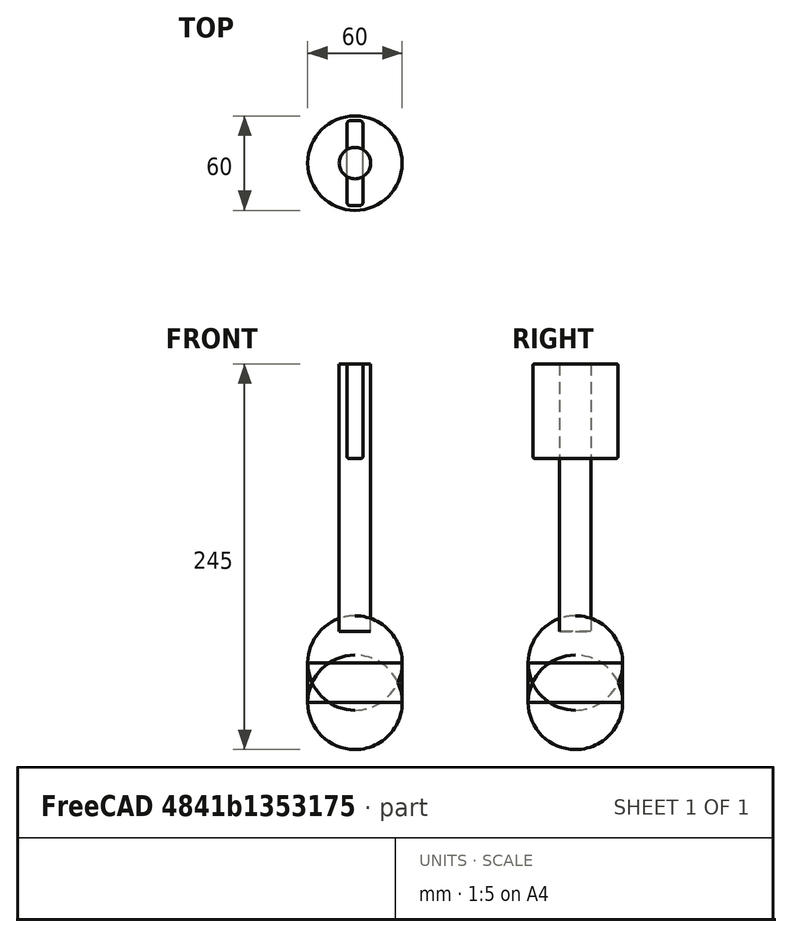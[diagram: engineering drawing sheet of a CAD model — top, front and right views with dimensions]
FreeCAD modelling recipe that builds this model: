
FCSTD DOCUMENT  (FreeCAD 0.20R29410 (Git))
Label: Spatule
License: All rights reserved
LicenseURL: http://en.wikipedia.org/wiki/All_rights_reserved
objects: Part::Sphere×2, Sketcher::SketchObject×1, PartDesign::Pad×1, PartDesign::Body×1, Part::Cylinder×1, Part::Box×1, Part::Fillet×1
note: 9 computed .brp shape members not serialized (recipe doc carries the construction recipe); baked Part::Feature solids carry a one-line shape summary decoded from their .brp

FEATURE [Sketcher::SketchObject] Sketch
  FullyConstrained = true
  MapMode = 5
  Support = -> [XY_Plane]
  sketch-geometry (1):
    g0: Circle CenterX=0 CenterY=0 CenterZ=0 NormalX=0 NormalY=0 NormalZ=1 AngleXU=0 Radius=30
  constraints (2):
    c: Coincident(g0,g-1)
    c: Radius(g0) = 30
FEATURE [PartDesign::Pad] Pad
  Direction = (0,0,1)
  Length = 25
  Length2 = 10
  Profile = -> Sketch
  ReferenceAxis = -> Sketch [N_Axis]
  Type = 0
FEATURE [PartDesign::Body] Body
  Group = -> [Sketch,Pad]
  Origin = -> Origin
  Tip = -> Pad
FEATURE [Part::Sphere] Sphere001
  Angle1 = -90
  Angle2 = 90
  Angle3 = 360
  AttacherType = Attacher::AttachEngine3D
  Placement = pos=(0,0,25) rot=(0,0,1;0rad)
  Radius = 30
FEATURE [Part::Cylinder] Cylinder
  Angle = 360
  AttacherType = Attacher::AttachEngine3D
  FirstAngle = 0
  Height = 170
  Placement = pos=(0,0,45) rot=(0,0,1;0rad)
  Radius = 10
  SecondAngle = 0
FEATURE [Part::Box] Box  label="Cube"
  AttacherType = Attacher::AttachEngine3D
  Height = 60
  Length = 10
  Placement = pos=(-5,-27,155) rot=(0,0,1;0rad)
  Width = 54
FEATURE [Part::Fillet] Fillet
  Base = -> Box
  Edges = 12 edges: [Edge1 r=2,Edge2 r=1,Edge3 r=2,Edge4 r=1,Edge5 r=2,Edge6 r=1,Edge7 r=2,Edge8 r=1,Edge9 r=1,Edge10 r=1,Edge11 r=1,Edge12 r=1]
FEATURE [Part::Sphere] Sphere
  Angle1 = -90
  Angle2 = 90
  Angle3 = 360
  AttacherType = Attacher::AttachEngine3D
  Radius = 30
